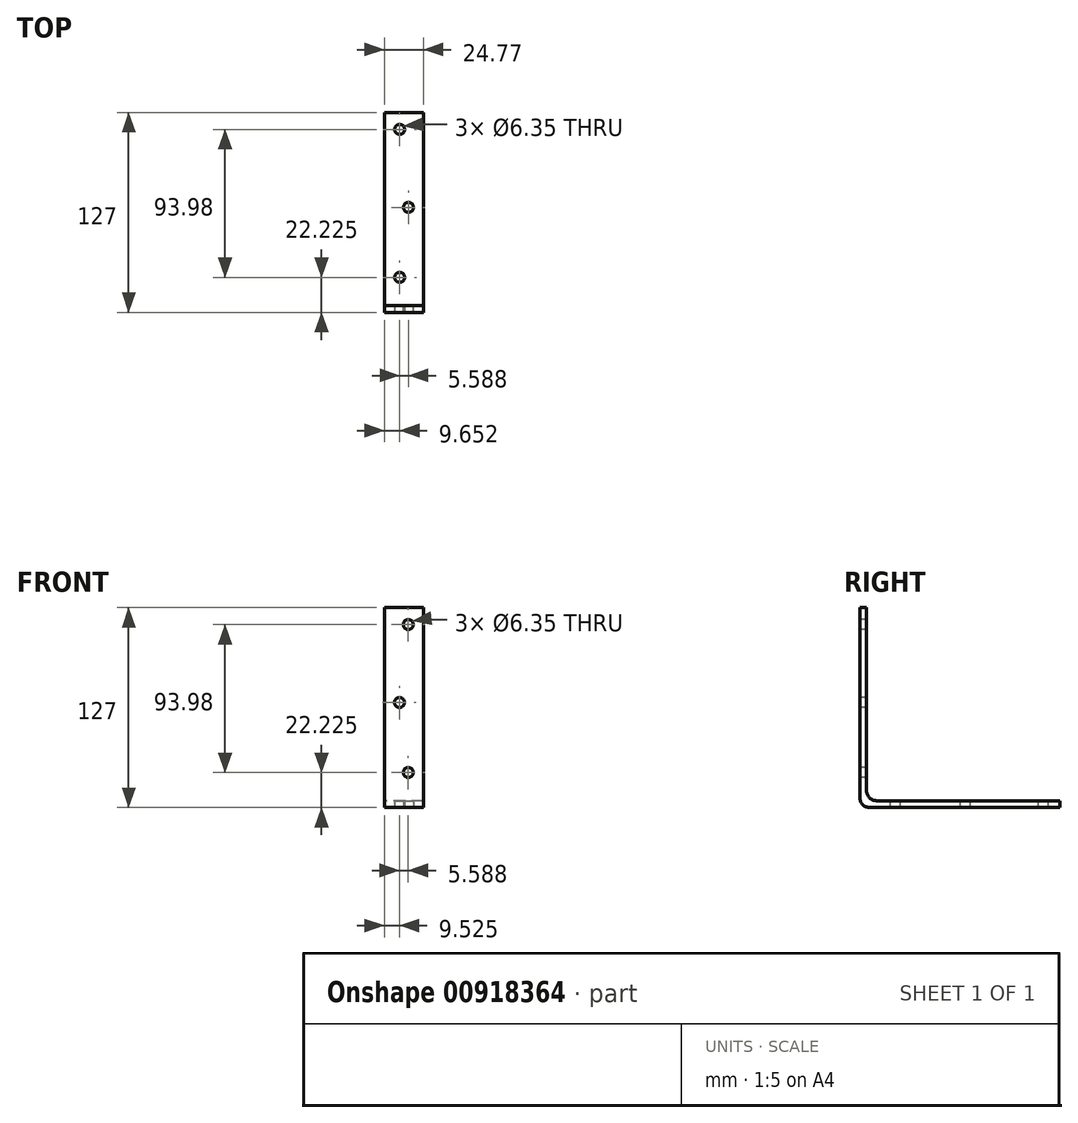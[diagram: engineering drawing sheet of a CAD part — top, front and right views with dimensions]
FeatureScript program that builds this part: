
annotation { "Feature Type Name" : "Feature", "Feature Type Description" : "" }
export const myFeature = defineFeature(function(context is Context, id is Id, definition is map)
    precondition{}
    {
        {
            var Q0;
            Q0=qCreatedBy(makeId("Right.planeOp"),FACE);
            var sketch = newSketch(context, id + "F0", { "sketchPlane" : qUnion([Q0])});
            skLineSegment(sketch, "E0", {"start": v(0, 0) * mm, "end": v(0, -127) * mm});
            skLineSegment(sketch, "E1", {"start": v(0, -127) * mm, "end": v(127, -127) * mm});
            skLineSegment(sketch, "E2", {"start": v(127, -127) * mm, "end": v(127, -122.68) * mm});
            skLineSegment(sketch, "E3", {"start": v(127, -122.68) * mm, "end": v(4.32, -122.68) * mm});
            skLineSegment(sketch, "E4", {"start": v(4.32, -122.68) * mm, "end": v(4.32, 0) * mm});
            skLineSegment(sketch, "E5", {"start": v(4.32, 0) * mm, "end": v(0, 0) * mm});
            skSolve(sketch);
        }
        {
            var Q0;
            Q0=makeQuery(id+"F0.imprint","IMPRINT",FACE,{"disambiguationData":[TD([[makeQuery(id+"F0.imprint","IMPRINT",EDGE,{"derivedFrom":sQuery(id+"F0.wireOp",EDGE,"E0")}),1.0]])]});
            extrude(context, id + "F1", {"entities" : qUnion([Q0]), "depth" : 24.76 * mm, "offsetDistance" : 25.4 * mm});
        }
        {
            var Q0;
            Q0=makeQuery(id+"F1.opExtrude","SWEPT_EDGE",EDGE,{"disambiguationData":[OSD([sQuery(id+"F0.wireOp",EDGE,"E3"),sQuery(id+"F0.wireOp",EDGE,"E4")])]});
            var Q1;
            Q1=makeQuery(id+"F1.opExtrude","SWEPT_EDGE",EDGE,{"disambiguationData":[OSD([sQuery(id+"F0.wireOp",EDGE,"E0"),sQuery(id+"F0.wireOp",EDGE,"E1")])]});
            fillet(context, id + "F2", {"entities" : qUnion([Q0, Q1]), "radius" : 6.35 * mm, "tangentPropagation" : true, "allowEdgeOverflow" : false});
        }
        {
            var Q0;
            Q0=makeQuery(id+"F1.opExtrude","SWEPT_FACE",FACE,{"disambiguationData":[OSD([sQuery(id+"F0.wireOp",EDGE,"E0")])]});
            var sketch = newSketch(context, id + "F3", { "sketchPlane" : qUnion([Q0])});
            skCircle(sketch, "E6", {"center": v(9.53, -60.32) * mm, "radius": 3.18 * mm});
            skCircle(sketch, "E7", {"center": v(15.11, -10.8) * mm, "radius": 3.18 * mm});
            skCircle(sketch, "E8", {"center": v(15.11, -104.78) * mm, "radius": 3.18 * mm});
            skSolve(sketch);
        }
        {
            var Q0;
            Q0=makeQuery(id+"F3.imprint","IMPRINT",FACE,{"disambiguationData":[TD([[makeQuery(id+"F3.imprint","IMPRINT",EDGE,{"derivedFrom":sQuery(id+"F3.wireOp",EDGE,"E8")}),1.0]])]});
            var Q1;
            Q1=makeQuery(id+"F3.imprint","IMPRINT",FACE,{"disambiguationData":[TD([[makeQuery(id+"F3.imprint","IMPRINT",EDGE,{"derivedFrom":sQuery(id+"F3.wireOp",EDGE,"E6")}),1.0]])]});
            var Q2;
            Q2=makeQuery(id+"F3.imprint","IMPRINT",FACE,{"disambiguationData":[TD([[makeQuery(id+"F3.imprint","IMPRINT",EDGE,{"derivedFrom":sQuery(id+"F3.wireOp",EDGE,"E7")}),1.0]])]});
            extrude(context, id + "F4", {"entities" : qUnion([Q0, Q1, Q2]), "operationType" : NewBodyOperationType.REMOVE, "endBound" : BoundingType.THROUGH_ALL, "oppositeDirection" : true, "depth" : 25.4 * mm, "offsetDistance" : 25.4 * mm});
        }
        {
            var Q0;
            Q0=makeQuery(id+"F1.opExtrude","SWEPT_FACE",FACE,{"disambiguationData":[OSD([sQuery(id+"F0.wireOp",EDGE,"E1")])]});
            var sketch = newSketch(context, id + "F5", { "sketchPlane" : qUnion([Q0])});
            skCircle(sketch, "E9", {"center": v(15.24, -66.68) * mm, "radius": 3.18 * mm});
            skCircle(sketch, "E10", {"center": v(9.65, -22.23) * mm, "radius": 3.18 * mm});
            skLineSegment(sketch, "E11", {"start": v(9.65, -22.23) * mm, "end": v(9.65, -91.45) * mm, "construction": true});
            skCircle(sketch, "E12", {"center": v(9.65, -116.2) * mm, "radius": 3.18 * mm});
            skSolve(sketch);
        }
        {
            var Q0;
            Q0=makeQuery(id+"F5.imprint","IMPRINT",FACE,{"disambiguationData":[TD([[makeQuery(id+"F5.imprint","IMPRINT",EDGE,{"derivedFrom":sQuery(id+"F5.wireOp",EDGE,"E12")}),1.0]])]});
            var Q1;
            Q1=makeQuery(id+"F5.imprint","IMPRINT",FACE,{"disambiguationData":[TD([[makeQuery(id+"F5.imprint","IMPRINT",EDGE,{"derivedFrom":sQuery(id+"F5.wireOp",EDGE,"E9")}),1.0]])]});
            var Q2;
            Q2=makeQuery(id+"F5.imprint","IMPRINT",FACE,{"disambiguationData":[TD([[makeQuery(id+"F5.imprint","IMPRINT",EDGE,{"derivedFrom":sQuery(id+"F5.wireOp",EDGE,"E10")}),1.0]])]});
            extrude(context, id + "F6", {"entities" : qUnion([Q0, Q1, Q2]), "operationType" : NewBodyOperationType.REMOVE, "endBound" : BoundingType.THROUGH_ALL, "oppositeDirection" : true, "depth" : 25.4 * mm, "offsetDistance" : 25.4 * mm});
        }
    });
